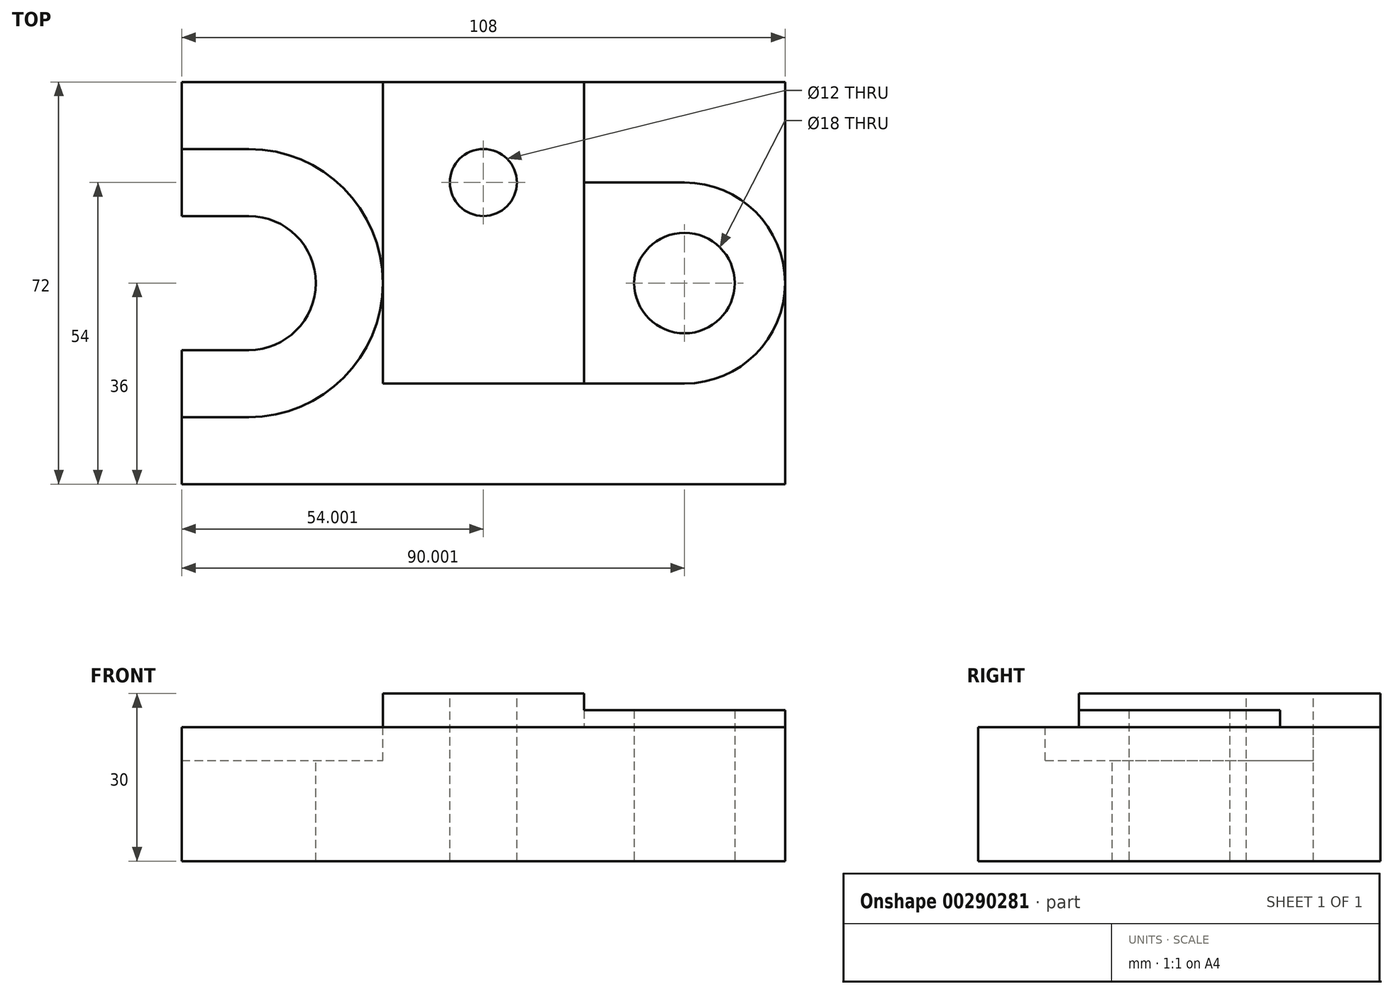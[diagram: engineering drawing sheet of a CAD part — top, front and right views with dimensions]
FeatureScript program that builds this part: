
annotation { "Feature Type Name" : "Feature", "Feature Type Description" : "" }
export const myFeature = defineFeature(function(context is Context, id is Id, definition is map)
    precondition{}
    {
        {
            var Q0;
            Q0=qCreatedBy(makeId("Front.planeOp"),FACE);
            var sketch = newSketch(context, id + "F0", { "sketchPlane" : qUnion([Q0])});
            skLineSegment(sketch, "E0", {"start": v(-50.37, 4.16) * mm, "end": v(-50.37, -19.84) * mm});
            skLineSegment(sketch, "E1", {"start": v(-50.37, -19.84) * mm, "end": v(57.63, -19.84) * mm});
            skLineSegment(sketch, "E2", {"start": v(57.63, -19.84) * mm, "end": v(57.63, 4.16) * mm});
            skLineSegment(sketch, "E3", {"start": v(57.63, 4.16) * mm, "end": v(-50.37, 4.16) * mm});
            skSolve(sketch);
        }
        {
            var Q0;
            Q0 = qSketchRegion(id + "F0", true);
            extrude(context, id + "F1", {"entities" : qUnion([Q0]), "depth" : 72 * mm});
        }
        {
            var Q0;
            Q0=makeQuery(id+"F1.opExtrude","SWEPT_FACE",FACE,{"disambiguationData":[OSD([sQuery(id+"F0.wireOp",EDGE,"E3")])]});
            var sketch = newSketch(context, id + "F2", { "sketchPlane" : qUnion([Q0])});
            skLineSegment(sketch, "E4", {"start": v(-50.37, -60) * mm, "end": v(-50.37, -48) * mm});
            skLineSegment(sketch, "E5", {"start": v(-50.37, -48) * mm, "end": v(-50.37, -24) * mm});
            skLineSegment(sketch, "E6", {"start": v(-50.37, -24) * mm, "end": v(-50.37, -12) * mm});
            skLineSegment(sketch, "E7", {"start": v(-50.37, -24) * mm, "end": v(-38.37, -24) * mm});
            skLineSegment(sketch, "E8", {"start": v(-50.37, -12) * mm, "end": v(-38.37, -12) * mm});
            skLineSegment(sketch, "E9", {"start": v(-50.37, -48) * mm, "end": v(-38.37, -48) * mm});
            skLineSegment(sketch, "E10", {"start": v(-50.37, -60) * mm, "end": v(-38.37, -60) * mm});
            skArc(sketch, "E11", {"start": v(-38.37, -60) * mm, "mid": v(-14.37, -36) * mm, "end": v(-38.37, -12) * mm});
            skArc(sketch, "E12", {"start": v(-38.37, -48) * mm, "mid": v(-26.37, -36) * mm, "end": v(-38.37, -24) * mm});
            skSolve(sketch);
        }
        {
            var Q0;
            Q0=makeQuery(id+"F2.imprint","IMPRINT",FACE,{"disambiguationData":[TD([[makeQuery(id+"F2.imprint","IMPRINT",EDGE,{"derivedFrom":sQuery(id+"F2.wireOp",EDGE,"E4")}),-1.0]])]});
            extrude(context, id + "F3", {"entities" : qUnion([Q0]), "operationType" : NewBodyOperationType.REMOVE, "oppositeDirection" : true, "depth" : 6 * mm});
        }
        {
            var Q0;
            Q0=makeQuery(id+"F3.boolean.opBoolean","SPLIT",FACE,{"disambiguationData":[TD([makeQuery(id+"F3.opExtrude","SWEPT_FACE",FACE,{"disambiguationData":[OSD([sQuery(id+"F2.wireOp",EDGE,"E7")])]})])],"derivedFrom":makeQuery(id+"F1.opExtrude","SWEPT_FACE",FACE,{"disambiguationData":[OSD([sQuery(id+"F0.wireOp",EDGE,"E3")])]})});
            extrude(context, id + "F4", {"entities" : qUnion([Q0]), "operationType" : NewBodyOperationType.REMOVE, "endBound" : BoundingType.THROUGH_ALL, "oppositeDirection" : true, "depth" : 25 * mm});
        }
        {
            var Q0;
            {var subQ0=sQuery(id+"F0.wireOp",EDGE,"E2");var subQ1=sQuery(id+"F0.wireOp",EDGE,"E3");Q0=makeQuery(id+"F3.boolean.opBoolean","SPLIT",FACE,{"disambiguationData":[TD([makeQuery(id+"F1.opExtrude","SWEPT_FACE",FACE,{"disambiguationData":[OSD([subQ0])]})])],"derivedFrom":makeQuery(id+"F1.opExtrude","SWEPT_FACE",FACE,{"disambiguationData":[OSD([subQ1])]})});}
            var sketch = newSketch(context, id + "F5", { "sketchPlane" : qUnion([Q0])});
            skLineSegment(sketch, "E13", {"start": v(-14.37, 0) * mm, "end": v(-14.37, -54) * mm});
            skPoint(sketch, "E13.startSnap0", {"position": v(-14.37, -36) * mm});
            skPoint(sketch, "E13.endSnap0", {"position": v(-14.37, -36) * mm});
            skLineSegment(sketch, "E14", {"start": v(-14.37, -54) * mm, "end": v(21.63, -54) * mm});
            skLineSegment(sketch, "E15", {"start": v(21.63, -54) * mm, "end": v(21.63, 0) * mm});
            skLineSegment(sketch, "E16", {"start": v(21.63, 0) * mm, "end": v(-14.37, 0) * mm});
            skSolve(sketch);
        }
        {
            var Q0;
            {var subQ0=sQuery(id+"F5.wireOp",EDGE,"E14");Q0=makeQuery(id+"F5.imprint","IMPRINT",FACE,{"disambiguationData":[TD([[makeQuery(id+"F5.imprint","IMPRINT",EDGE,{"derivedFrom":subQ0}),1.0]])]});}
            extrude(context, id + "F6", {"entities" : qUnion([Q0]), "operationType" : NewBodyOperationType.ADD, "depth" : 6 * mm});
        }
        {
            var Q0;
            Q0=makeQuery(id+"F6.opExtrude","CAP_FACE",FACE,{"disambiguationData":[OSD([sQuery(id+"F5.wireOp",EDGE,"E13"),sQuery(id+"F5.wireOp",EDGE,"E14"),sQuery(id+"F5.wireOp",EDGE,"E15"),sQuery(id+"F5.wireOp",EDGE,"E16")])],"isStart":false});
            var sketch = newSketch(context, id + "F7", { "sketchPlane" : qUnion([Q0])});
            skLineSegment(sketch, "E17", {"start": v(3.63, -12) * mm, "end": v(3.63, -18) * mm});
            skPoint(sketch, "E17.endSnap0", {"position": v(3.63, 0) * mm});
            skCircle(sketch, "E18", {"center": v(3.63, -18) * mm, "radius": 6 * mm});
            skSolve(sketch);
        }
        {
            var Q0;
            Q0 = qSketchRegion(id + "F7", true);
            extrude(context, id + "F8", {"entities" : qUnion([Q0]), "operationType" : NewBodyOperationType.REMOVE, "endBound" : BoundingType.THROUGH_ALL, "oppositeDirection" : true, "depth" : 25 * mm});
        }
        {
            var Q0;
            {var subQ2=sQuery(id+"F0.wireOp",EDGE,"E3");var subQ3=makeQuery(id+"F1.opExtrude","SWEPT_FACE",FACE,{"disambiguationData":[OSD([subQ2])]});var subQ6=sQuery(id+"F0.wireOp",EDGE,"E2");var subQ10=makeQuery(id+"F1.opExtrude","SWEPT_FACE",FACE,{"disambiguationData":[OSD([subQ6])]});Q0=makeQuery(id+"F6.boolean.opBoolean","SPLIT",FACE,{"disambiguationData":[TD([subQ10])],"derivedFrom":makeQuery(id+"F3.boolean.opBoolean","SPLIT",FACE,{"disambiguationData":[TD([subQ10])],"derivedFrom":subQ3})});}
            var sketch = newSketch(context, id + "F9", { "sketchPlane" : qUnion([Q0])});
            skPoint(sketch, "E19.startSnap0", {"position": v(3.63, -54) * mm});
            skCircle(sketch, "E20", {"center": v(39.63, -36) * mm, "radius": 9 * mm});
            skArc(sketch, "E21", {"start": v(39.63, -54) * mm, "mid": v(57.63, -36) * mm, "end": v(39.63, -18) * mm});
            skArc(sketch, "E22", {"start": v(39.63, -18) * mm, "mid": v(57.63, -36) * mm, "end": v(39.63, -54) * mm});
            skLineSegment(sketch, "E23", {"start": v(39.63, -18) * mm, "end": v(21.63, -18) * mm});
            skLineSegment(sketch, "E24", {"start": v(39.63, -54) * mm, "end": v(21.63, -54) * mm});
            skLineSegment(sketch, "E25", {"start": v(21.63, -18) * mm, "end": v(21.63, -54) * mm});
            skSolve(sketch);
        }
        {
            var Q0;
            Q0 = qSketchRegion(id + "F9", true);
            extrude(context, id + "F10", {"entities" : qUnion([Q0]), "operationType" : NewBodyOperationType.ADD, "depth" : 3 * mm});
        }
        {
            var Q0;
            {var subQ2=sQuery(id+"F0.wireOp",EDGE,"E3");var subQ3=makeQuery(id+"F1.opExtrude","SWEPT_FACE",FACE,{"disambiguationData":[OSD([subQ2])]});var subQ6=sQuery(id+"F0.wireOp",EDGE,"E2");var subQ10=makeQuery(id+"F1.opExtrude","SWEPT_FACE",FACE,{"disambiguationData":[OSD([subQ6])]});Q0=makeQuery(id+"F10.boolean.opBoolean","SPLIT",FACE,{"disambiguationData":[TD([makeQuery(id+"F10.opExtrude","SWEPT_FACE",FACE,{"disambiguationData":[OSD([sQuery(id+"F9.wireOp",EDGE,"E20")])]})])],"derivedFrom":makeQuery(id+"F6.boolean.opBoolean","SPLIT",FACE,{"disambiguationData":[TD([subQ10])],"derivedFrom":makeQuery(id+"F3.boolean.opBoolean","SPLIT",FACE,{"disambiguationData":[TD([subQ10])],"derivedFrom":subQ3})})});}
            extrude(context, id + "F11", {"entities" : qUnion([Q0]), "operationType" : NewBodyOperationType.REMOVE, "endBound" : BoundingType.THROUGH_ALL, "oppositeDirection" : true, "depth" : 25 * mm});
        }
    });
